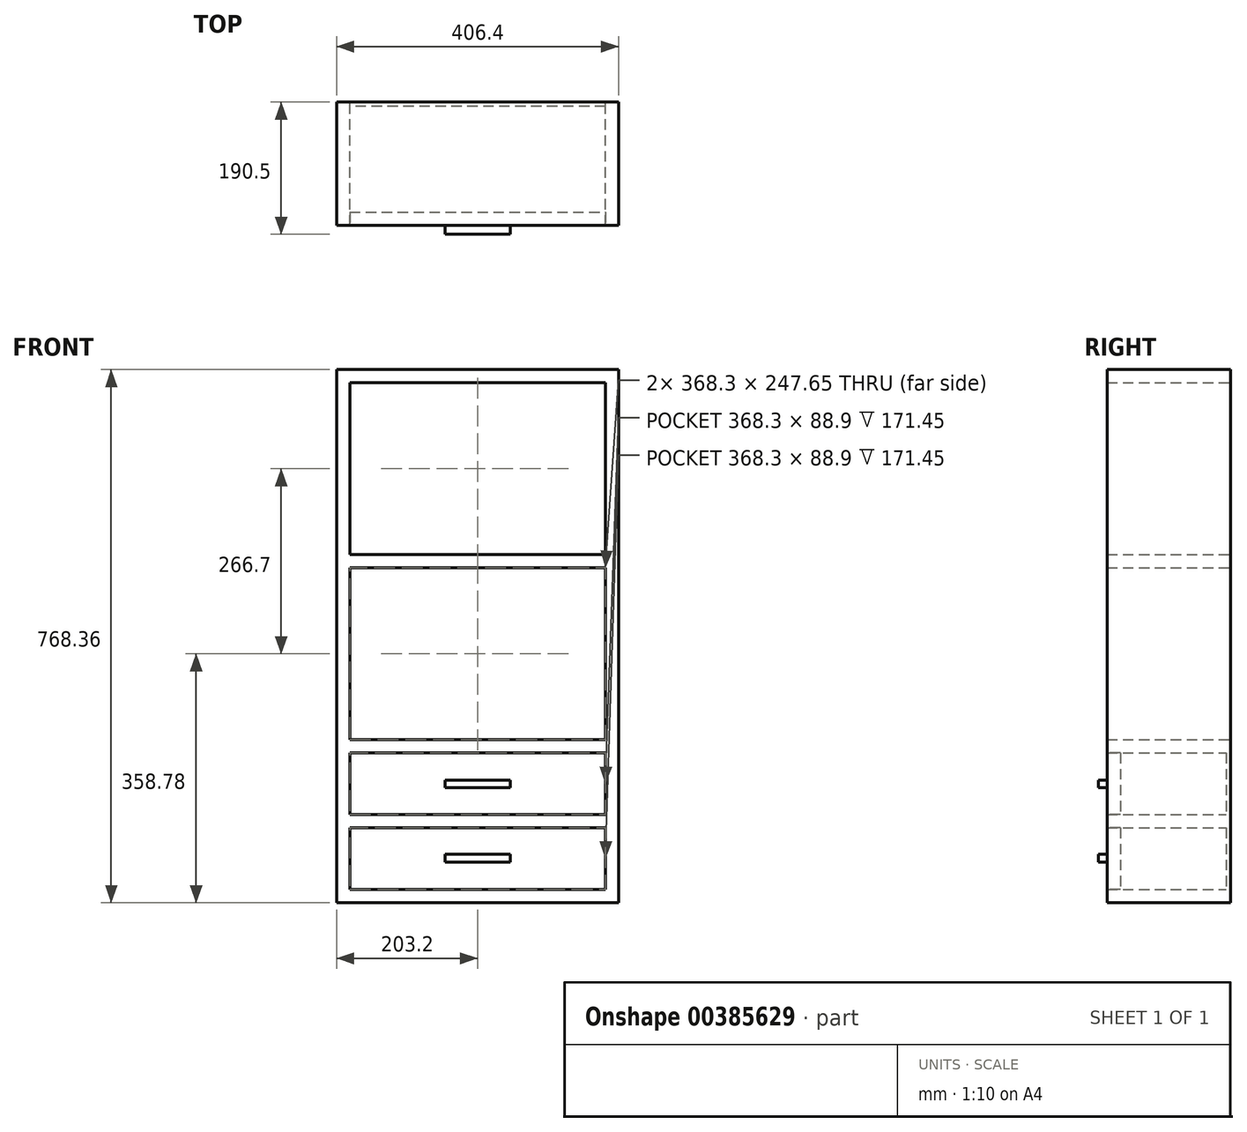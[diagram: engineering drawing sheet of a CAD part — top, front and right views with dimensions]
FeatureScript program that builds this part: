
annotation { "Feature Type Name" : "Feature", "Feature Type Description" : "" }
export const myFeature = defineFeature(function(context is Context, id is Id, definition is map)
    precondition{}
    {
        {
            var Q0;
            Q0=qCreatedBy(makeId("Front.planeOp"),FACE);
            var sketch = newSketch(context, id + "F0", { "sketchPlane" : qUnion([Q0])});
            skLineSegment(sketch, "E0.bottom", {"start": v(-203.2, 384.18) * mm, "end": v(203.2, 384.18) * mm});
            skLineSegment(sketch, "E0.top", {"start": v(-203.2, -384.18) * mm, "end": v(203.2, -384.18) * mm});
            skLineSegment(sketch, "E0.left", {"start": v(-203.2, 384.18) * mm, "end": v(-203.2, -384.18) * mm});
            skLineSegment(sketch, "E0.right", {"start": v(203.2, 384.18) * mm, "end": v(203.2, -384.18) * mm});
            skPoint(sketch, "E0.middle", {"position": v(0, 0) * mm});
            skLineSegment(sketch, "E1.0", {"start": v(-184.15, 365.13) * mm, "end": v(184.15, 365.13) * mm});
            skLineSegment(sketch, "E1.1", {"start": v(-184.15, 365.13) * mm, "end": v(-184.15, -365.13) * mm});
            skLineSegment(sketch, "E1.2", {"start": v(-184.15, -365.13) * mm, "end": v(184.15, -365.13) * mm});
            skLineSegment(sketch, "E1.3", {"start": v(184.15, 365.13) * mm, "end": v(184.15, -365.13) * mm});
            skLineSegment(sketch, "E2.bottom", {"start": v(-184.15, -257.18) * mm, "end": v(184.15, -257.18) * mm});
            skLineSegment(sketch, "E2.top", {"start": v(-184.15, -276.23) * mm, "end": v(184.15, -276.23) * mm});
            skLineSegment(sketch, "E2.left", {"start": v(-184.15, -257.18) * mm, "end": v(-184.15, -276.23) * mm});
            skLineSegment(sketch, "E2.right", {"start": v(184.15, -257.18) * mm, "end": v(184.15, -276.23) * mm});
            skLineSegment(sketch, "E3.bottom", {"start": v(-184.15, -149.22) * mm, "end": v(184.15, -149.22) * mm});
            skLineSegment(sketch, "E3.top", {"start": v(-184.15, -168.28) * mm, "end": v(184.15, -168.28) * mm});
            skLineSegment(sketch, "E3.left", {"start": v(-184.15, -149.22) * mm, "end": v(-184.15, -168.28) * mm});
            skLineSegment(sketch, "E3.right", {"start": v(184.15, -149.22) * mm, "end": v(184.15, -168.28) * mm});
            skLineSegment(sketch, "E4.bottom", {"start": v(-184.15, 117.48) * mm, "end": v(184.15, 117.48) * mm});
            skLineSegment(sketch, "E4.top", {"start": v(-184.15, 98.43) * mm, "end": v(184.15, 98.43) * mm});
            skLineSegment(sketch, "E4.left", {"start": v(-184.15, 117.48) * mm, "end": v(-184.15, 98.43) * mm});
            skLineSegment(sketch, "E4.right", {"start": v(184.15, 117.48) * mm, "end": v(184.15, 98.43) * mm});
            skSolve(sketch);
        }
        {
            var Q0;
            Q0=makeQuery(id+"F0.imprint","IMPRINT",FACE,{"disambiguationData":[TD([[makeQuery(id+"F0.imprint","IMPRINT",EDGE,{"derivedFrom":sQuery(id+"F0.wireOp",EDGE,"E0.bottom")}),-1.0]])]});
            var Q1;
            {var subQ2=sQuery(id+"F0.wireOp",EDGE,"E4.bottom");Q1=makeQuery(id+"F0.imprint","IMPRINT",FACE,{"disambiguationData":[TD([[makeQuery(id+"F0.imprint","IMPRINT",EDGE,{"derivedFrom":subQ2}),-1.0]])]});}
            var Q2;
            {var subQ0=sQuery(id+"F0.wireOp",EDGE,"E3.bottom");Q2=makeQuery(id+"F0.imprint","IMPRINT",FACE,{"disambiguationData":[TD([[makeQuery(id+"F0.imprint","IMPRINT",EDGE,{"derivedFrom":subQ0}),-1.0]])]});}
            var Q3;
            {var subQ2=sQuery(id+"F0.wireOp",EDGE,"E2.bottom");Q3=makeQuery(id+"F0.imprint","IMPRINT",FACE,{"disambiguationData":[TD([[makeQuery(id+"F0.imprint","IMPRINT",EDGE,{"derivedFrom":subQ2}),-1.0]])]});}
            extrude(context, id + "F1", {"entities" : qUnion([Q0, Q1, Q2, Q3]), "depth" : 177.8 * mm, "offsetDistance" : 25.4 * mm});
        }
        {
            var Q0;
            Q0=makeQuery(id+"F1.opExtrude","CAP_FACE",FACE,{"disambiguationData":[OSD([sQuery(id+"F0.wireOp",EDGE,"E0.bottom"),sQuery(id+"F0.wireOp",EDGE,"E0.top"),sQuery(id+"F0.wireOp",EDGE,"E0.left"),sQuery(id+"F0.wireOp",EDGE,"E0.right"),sQuery(id+"F0.wireOp",EDGE,"E1.0"),sQuery(id+"F0.wireOp",EDGE,"E1.1"),sQuery(id+"F0.wireOp",EDGE,"E1.2"),sQuery(id+"F0.wireOp",EDGE,"E1.3"),sQuery(id+"F0.wireOp",EDGE,"E2.bottom"),sQuery(id+"F0.wireOp",EDGE,"E2.top"),sQuery(id+"F0.wireOp",EDGE,"E3.bottom"),sQuery(id+"F0.wireOp",EDGE,"E3.top"),sQuery(id+"F0.wireOp",EDGE,"E4.bottom"),sQuery(id+"F0.wireOp",EDGE,"E4.top")])],"isStart":false});
            var sketch = newSketch(context, id + "F2", { "sketchPlane" : qUnion([Q0])});
            skLineSegment(sketch, "E5.0", {"start": v(-184.15, -168.28) * mm, "end": v(184.15, -168.28) * mm});
            skLineSegment(sketch, "E6.0", {"start": v(-184.15, -168.28) * mm, "end": v(-184.15, -257.18) * mm});
            skLineSegment(sketch, "E7.0", {"start": v(-184.15, -257.18) * mm, "end": v(184.15, -257.18) * mm});
            skLineSegment(sketch, "E8.0", {"start": v(184.15, -168.28) * mm, "end": v(184.15, -257.18) * mm});
            skLineSegment(sketch, "E9.0", {"start": v(-184.15, -276.23) * mm, "end": v(184.15, -276.23) * mm});
            skLineSegment(sketch, "E10.0", {"start": v(-184.15, -276.23) * mm, "end": v(-184.15, -365.13) * mm});
            skLineSegment(sketch, "E11.0", {"start": v(-184.15, -365.13) * mm, "end": v(184.15, -365.13) * mm});
            skLineSegment(sketch, "E12.0", {"start": v(184.15, -276.23) * mm, "end": v(184.15, -365.13) * mm});
            skSolve(sketch);
        }
        {
            var Q0;
            Q0 = qSketchRegion(id + "F2", true);
            extrude(context, id + "F3", {"entities" : qUnion([Q0]), "oppositeDirection" : true, "depth" : 19.05 * mm, "offsetDistance" : 25.4 * mm});
        }
        {
            var Q0;
            Q0=makeQuery(id+"F3.opExtrude","CAP_FACE",FACE,{"disambiguationData":[OSD([sQuery(id+"F2.wireOp",EDGE,"E5.0"),sQuery(id+"F2.wireOp",EDGE,"E6.0"),sQuery(id+"F2.wireOp",EDGE,"E7.0"),sQuery(id+"F2.wireOp",EDGE,"E8.0")])],"isStart":true});
            var sketch = newSketch(context, id + "F4", { "sketchPlane" : qUnion([Q0])});
            skLineSegment(sketch, "E13.bottom", {"start": v(-46.79, -207.17) * mm, "end": v(46.79, -207.17) * mm});
            skLineSegment(sketch, "E13.top", {"start": v(-46.79, -218.28) * mm, "end": v(46.79, -218.28) * mm});
            skLineSegment(sketch, "E13.left", {"start": v(-46.79, -207.17) * mm, "end": v(-46.79, -218.28) * mm});
            skLineSegment(sketch, "E13.right", {"start": v(46.79, -207.17) * mm, "end": v(46.79, -218.28) * mm});
            skPoint(sketch, "E13.middle", {"position": v(0, -212.73) * mm});
            skPoint(sketch, "E13.middle.positionSnap0", {"position": v(-184.15, -212.73) * mm});
            skPoint(sketch, "E13.middle.positionSnap1", {"position": v(0, -168.28) * mm});
            skPoint(sketch, "E13.centerSnap0", {"position": v(-184.15, -212.73) * mm});
            skPoint(sketch, "E13.centerSnap1", {"position": v(0, -168.28) * mm});
            skLineSegment(sketch, "E14", {"start": v(-274.3, -266.27) * mm, "end": v(245.1, -266.27) * mm, "construction": true});
            skLineSegment(sketch, "E15.MirrorCS", {"start": v(-46.79, -314.25) * mm, "end": v(46.79, -314.25) * mm});
            skLineSegment(sketch, "E16.MirrorCS", {"start": v(-46.79, -325.37) * mm, "end": v(46.79, -325.37) * mm});
            skLineSegment(sketch, "E17.MirrorCS", {"start": v(46.79, -325.37) * mm, "end": v(46.79, -314.25) * mm});
            skLineSegment(sketch, "E18.MirrorCS", {"start": v(-46.79, -325.37) * mm, "end": v(-46.79, -314.25) * mm});
            skSolve(sketch);
        }
        {
            var Q0;
            Q0=makeQuery(id+"F4.imprint","IMPRINT",FACE,{"disambiguationData":[TD([[makeQuery(id+"F4.imprint","IMPRINT",EDGE,{"derivedFrom":sQuery(id+"F4.wireOp",EDGE,"E13.bottom")}),-1.0]])]});
            var Q1;
            Q1=makeQuery(id+"F4.imprint","IMPRINT",FACE,{"disambiguationData":[TD([[makeQuery(id+"F4.imprint","IMPRINT",EDGE,{"derivedFrom":sQuery(id+"F4.wireOp",EDGE,"E15.MirrorCS")}),-1.0]])]});
            extrude(context, id + "F5", {"entities" : qUnion([Q0, Q1]), "operationType" : NewBodyOperationType.ADD, "depth" : 12.7 * mm, "offsetDistance" : 25.4 * mm});
        }
        {
            var Q0;
            Q0=makeQuery(id+"F1.opExtrude","CAP_FACE",FACE,{"disambiguationData":[OSD([sQuery(id+"F0.wireOp",EDGE,"E0.bottom"),sQuery(id+"F0.wireOp",EDGE,"E0.top"),sQuery(id+"F0.wireOp",EDGE,"E0.left"),sQuery(id+"F0.wireOp",EDGE,"E0.right"),sQuery(id+"F0.wireOp",EDGE,"E1.0"),sQuery(id+"F0.wireOp",EDGE,"E1.1"),sQuery(id+"F0.wireOp",EDGE,"E1.2"),sQuery(id+"F0.wireOp",EDGE,"E1.3"),sQuery(id+"F0.wireOp",EDGE,"E2.bottom"),sQuery(id+"F0.wireOp",EDGE,"E2.top"),sQuery(id+"F0.wireOp",EDGE,"E3.bottom"),sQuery(id+"F0.wireOp",EDGE,"E3.top"),sQuery(id+"F0.wireOp",EDGE,"E4.bottom"),sQuery(id+"F0.wireOp",EDGE,"E4.top")])],"isStart":true});
            var sketch = newSketch(context, id + "F6", { "sketchPlane" : qUnion([Q0])});
            skLineSegment(sketch, "E19.bottom", {"start": v(-184.15, -168.28) * mm, "end": v(184.15, -168.28) * mm});
            skLineSegment(sketch, "E19.top", {"start": v(-184.15, -365.13) * mm, "end": v(184.15, -365.13) * mm});
            skLineSegment(sketch, "E19.left", {"start": v(-184.15, -168.28) * mm, "end": v(-184.15, -365.13) * mm});
            skLineSegment(sketch, "E19.right", {"start": v(184.15, -168.28) * mm, "end": v(184.15, -365.13) * mm});
            skSolve(sketch);
        }
        {
            var Q0;
            Q0 = qSketchRegion(id + "F6", true);
            extrude(context, id + "F7", {"entities" : qUnion([Q0]), "operationType" : NewBodyOperationType.ADD, "oppositeDirection" : true, "depth" : 6.35 * mm, "offsetDistance" : 25.4 * mm});
        }
    });
